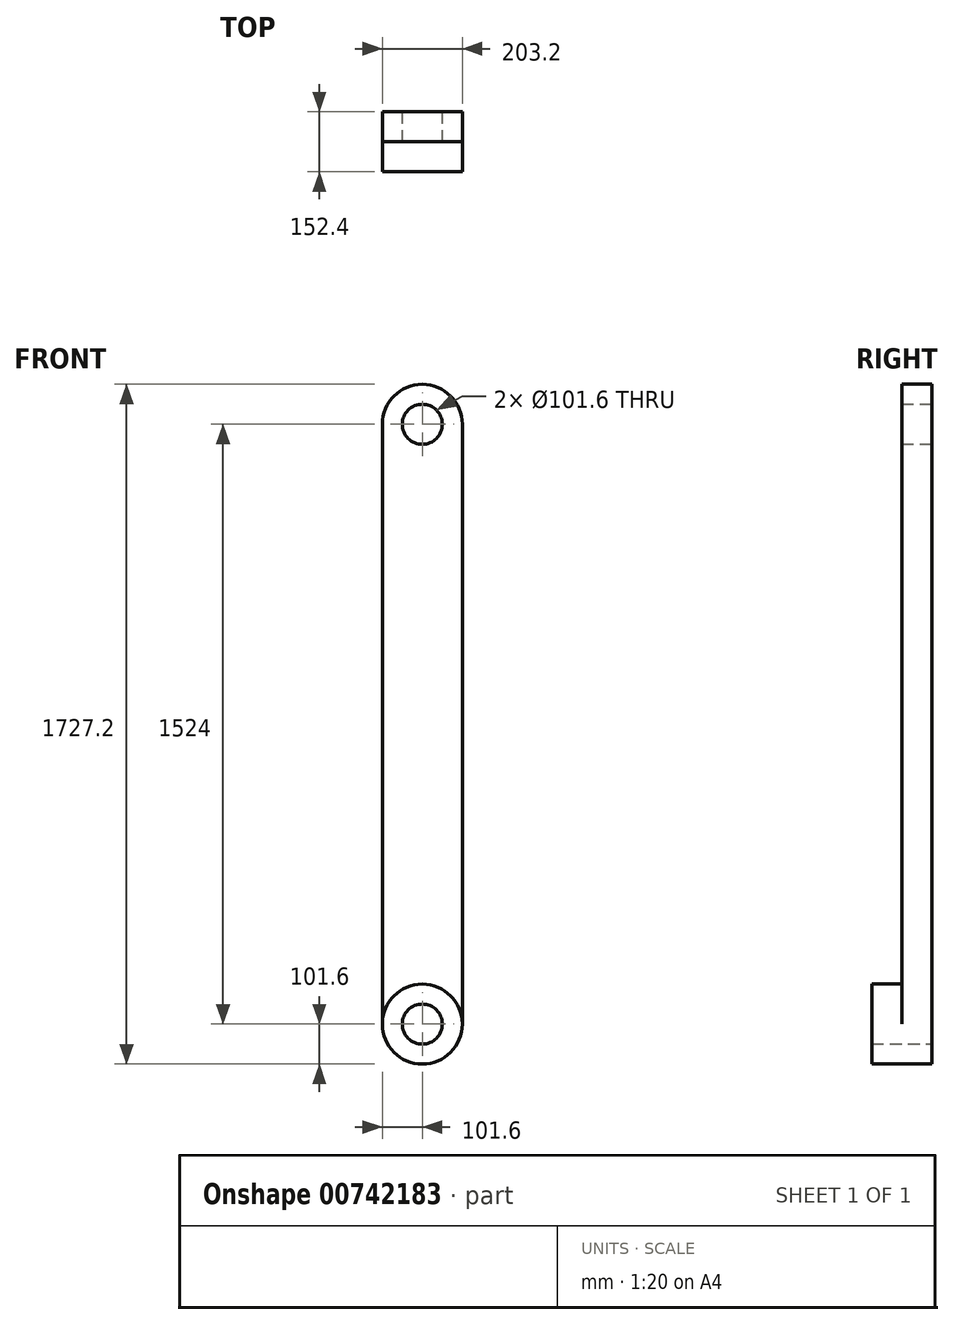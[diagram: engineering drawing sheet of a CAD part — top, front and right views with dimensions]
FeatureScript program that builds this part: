
annotation { "Feature Type Name" : "Feature", "Feature Type Description" : "" }
export const myFeature = defineFeature(function(context is Context, id is Id, definition is map)
    precondition{}
    {
        {
            var Q0;
            Q0=qCreatedBy(makeId("Front.planeOp"),FACE);
            var sketch = newSketch(context, id + "F0", { "sketchPlane" : qUnion([Q0])});
            skLineSegment(sketch, "E0.bottom", {"start": v(0, -101.6) * mm, "end": v(0, -101.6) * mm});
            skLineSegment(sketch, "E0.top", {"start": v(0, 1625.6) * mm, "end": v(0, 1625.6) * mm});
            skLineSegment(sketch, "E0.left", {"start": v(-101.6, 0) * mm, "end": v(-101.6, 1524) * mm});
            skLineSegment(sketch, "E0.right", {"start": v(101.6, 0) * mm, "end": v(101.6, 1524) * mm});
            skPoint(sketch, "E1.visualSharp", {"position": v(-101.6, 1625.6) * mm});
            skArc(sketch, "E1.filletArc", {"start": v(0, 1625.6) * mm, "mid": v(-71.84, 1595.84) * mm, "end": v(-101.6, 1524) * mm});
            skPoint(sketch, "E2.visualSharp", {"position": v(-101.6, -101.6) * mm});
            skArc(sketch, "E2.filletArc", {"start": v(-101.6, 0) * mm, "mid": v(-71.84, -71.84) * mm, "end": v(0, -101.6) * mm});
            skPoint(sketch, "E3.visualSharp", {"position": v(101.6, -101.6) * mm});
            skArc(sketch, "E3.filletArc", {"start": v(0, -101.6) * mm, "mid": v(71.84, -71.84) * mm, "end": v(101.6, 0) * mm});
            skPoint(sketch, "E4.visualSharp", {"position": v(101.6, 1625.6) * mm});
            skArc(sketch, "E4.filletArc", {"start": v(101.6, 1524) * mm, "mid": v(71.84, 1595.84) * mm, "end": v(0, 1625.6) * mm});
            skCircle(sketch, "E5", {"center": v(0, 1524) * mm, "radius": 50.8 * mm});
            skCircle(sketch, "E6", {"center": v(0, 0) * mm, "radius": 50.8 * mm});
            skSolve(sketch);
        }
        {
            var Q0;
            Q0 = qSketchRegion(id + "F0", true);
            extrude(context, id + "F1", {"entities" : qUnion([Q0]), "depth" : 76.2 * mm, "offsetDistance" : 25.4 * mm});
        }
        {
            var Q0;
            Q0=makeQuery(id+"F1.opExtrude","CAP_FACE",FACE,{"disambiguationData":[OSD([sQuery(id+"F0.wireOp",EDGE,"E0.left"),sQuery(id+"F0.wireOp",EDGE,"E0.right"),sQuery(id+"F0.wireOp",EDGE,"E1.filletArc"),sQuery(id+"F0.wireOp",EDGE,"E2.filletArc"),sQuery(id+"F0.wireOp",EDGE,"E3.filletArc"),sQuery(id+"F0.wireOp",EDGE,"E4.filletArc"),sQuery(id+"F0.wireOp",EDGE,"E5"),sQuery(id+"F0.wireOp",EDGE,"E6")])],"isStart":false});
            var sketch = newSketch(context, id + "F2", { "sketchPlane" : qUnion([Q0])});
            skCircle(sketch, "E7", {"center": v(0, 0) * mm, "radius": 101.6 * mm});
            skCircle(sketch, "E8", {"center": v(0, 0) * mm, "radius": 50.8 * mm});
            skSolve(sketch);
        }
        {
            var Q0;
            Q0 = qSketchRegion(id + "F2", true);
            extrude(context, id + "F3", {"entities" : qUnion([Q0]), "operationType" : NewBodyOperationType.ADD, "depth" : 76.2 * mm, "offsetDistance" : 25.4 * mm});
        }
    });
